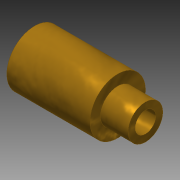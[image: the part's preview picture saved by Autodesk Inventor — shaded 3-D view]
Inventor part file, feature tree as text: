
AUTODESK INVENTOR PART (.ipt)
format: ipt  version: 2014 (Build 180170000, 170)  size: 94,720 bytes
history: native  units: mm
features: extrude x2, sketch x2, other x1
ambient origin geometry x8: Origin, YZ Plane, XZ Plane, XY Plane, X Axis, Y Axis, Z Axis, Center Point
bodies: Body1 (feature_tree)
feature tree (5):
  other  "Твердое тело1"
  extrude  "Выдавливание1"  Depth=3.0mm
  extrude  "Выдавливание2"  Depth=8.0mm
  sketch  "Эскиз1"
  sketch  "Эскиз2"
